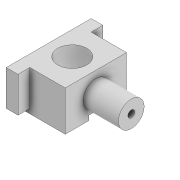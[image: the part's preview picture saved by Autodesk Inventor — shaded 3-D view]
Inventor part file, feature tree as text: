
AUTODESK INVENTOR PART (.ipt)
format: ipt  version: 2022 (Build 260153000, 153)  size: 166,400 bytes
history: native  units: mm
features: extrude x6, sketch x6, projected_geometry x1
ambient origin geometry x8: Origin, YZ Plane, XZ Plane, XY Plane, X Axis, Y Axis, Z Axis, Center Point
bodies: Solid1 (feature_tree)
feature tree (13):
  extrude  "Extrusion1"  Depth=10.0mm
  extrude  "Extrusion2"  Depth=10.0mm
  sketch  "Sketch3"  dims[d4=13.0mm d5=15.0mm d6=0.0mm]
  extrude  "Extrusion3"  Depth=15.0mm TaperAngle=0.0deg
  extrude  "Extrusion6"  Depth=6.5mm
  extrude  "Extrusion7"  Depth=55.0mm TaperAngle=0.0deg
  extrude  "Extrusion8"  Depth=15.0mm TaperAngle=0.0deg
  sketch  "Sketch1"  dims[d0=12.3mm d1=10.0mm]
  sketch  "Sketch2"  dims[d2=10.0mm d3=13.0mm]
  projected_geometry  "Projected Loop1"
  sketch  "Sketch6"  dims[d7=2.9mm d8=6.5mm]
  sketch  "Sketch7"  dims[d11=13.0mm d13=55.0mm d14=0.0mm]
  sketch  "Sketch8"  dims[d16=4.0mm d17=15.0mm d18=0.0mm d21=3.2mm d22=3.2mm d23=4.0mm d24=4.0mm d31=5.0mm d32=5.0mm d33=0.0mm d34=5.0mm d35=5.0mm d36=0.0mm d37=10.0mm d38=10.0mm d39=2.0mm d40=0.0mm]
